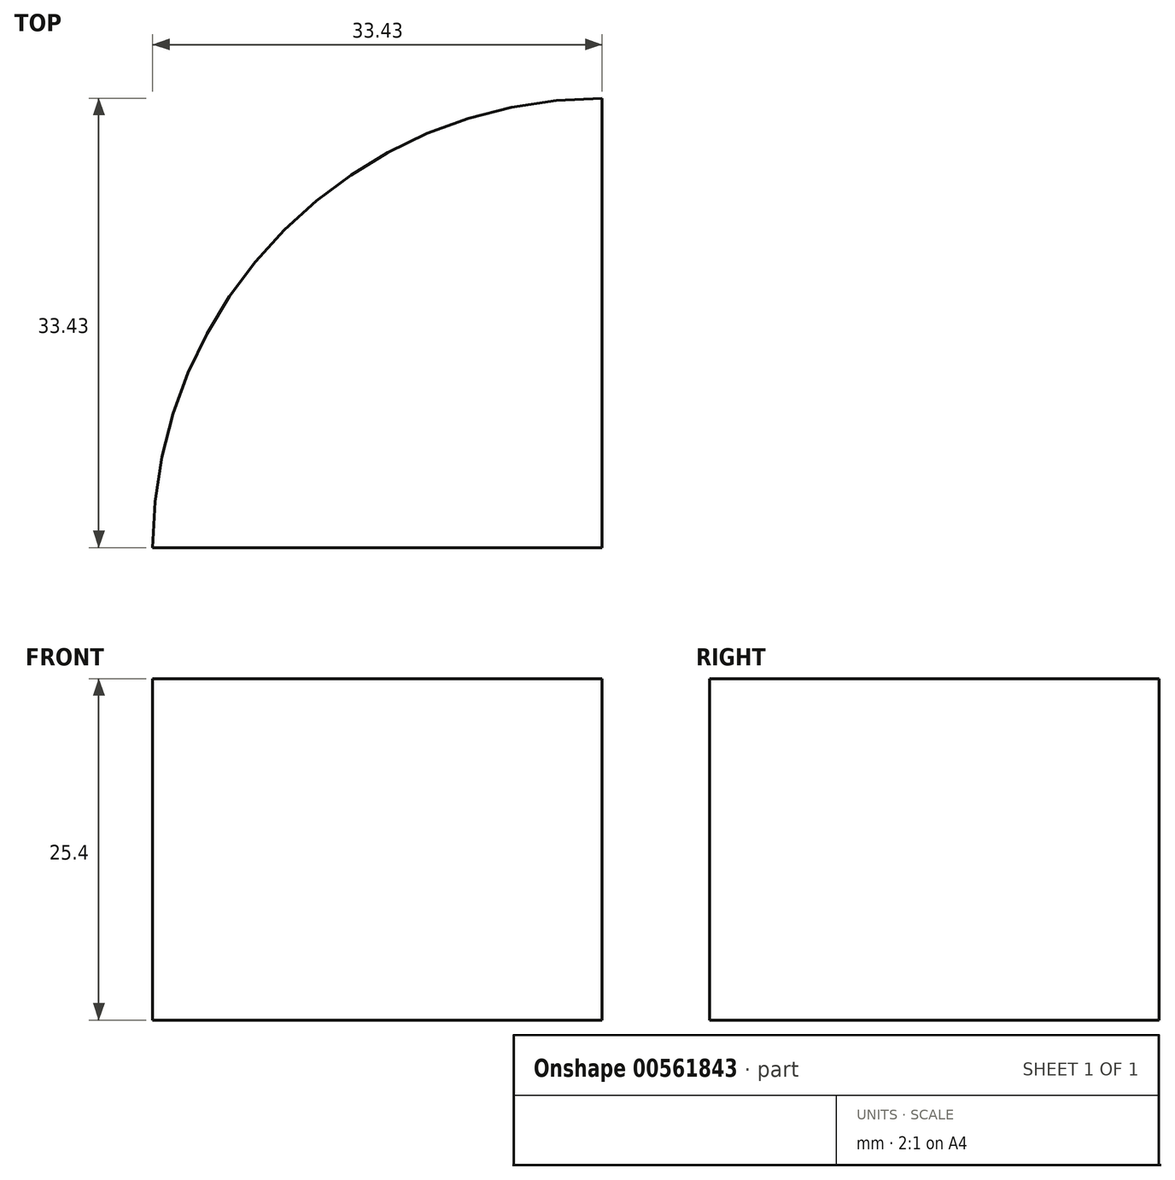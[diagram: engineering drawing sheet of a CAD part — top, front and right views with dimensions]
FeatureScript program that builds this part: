
annotation { "Feature Type Name" : "Feature", "Feature Type Description" : "" }
export const myFeature = defineFeature(function(context is Context, id is Id, definition is map)
    precondition{}
    {
        {
            var Q0;
            Q0=qCreatedBy(makeId("Top.planeOp"),FACE);
            var sketch = newSketch(context, id + "F0", { "sketchPlane" : qUnion([Q0])});
            skArc(sketch, "E0", {"start": v(0, 33.43) * mm, "mid": v(-23.64, 23.64) * mm, "end": v(-33.43, 0) * mm});
            skLineSegment(sketch, "E1", {"start": v(-33.43, 0) * mm, "end": v(0, 0) * mm});
            skLineSegment(sketch, "E2", {"start": v(0, 0) * mm, "end": v(0, 33.43) * mm});
            skSolve(sketch);
        }
        {
            var Q0;
            Q0=makeQuery(id+"F0.imprint","IMPRINT",FACE,{"disambiguationData":[TD([[makeQuery(id+"F0.imprint","IMPRINT",EDGE,{"derivedFrom":sQuery(id+"F0.wireOp",EDGE,"E0")}),1.0]])]});
            extrude(context, id + "F1", {"entities" : qUnion([Q0]), "depth" : 25.4 * mm, "offsetDistance" : 25.4 * mm});
        }
    });
